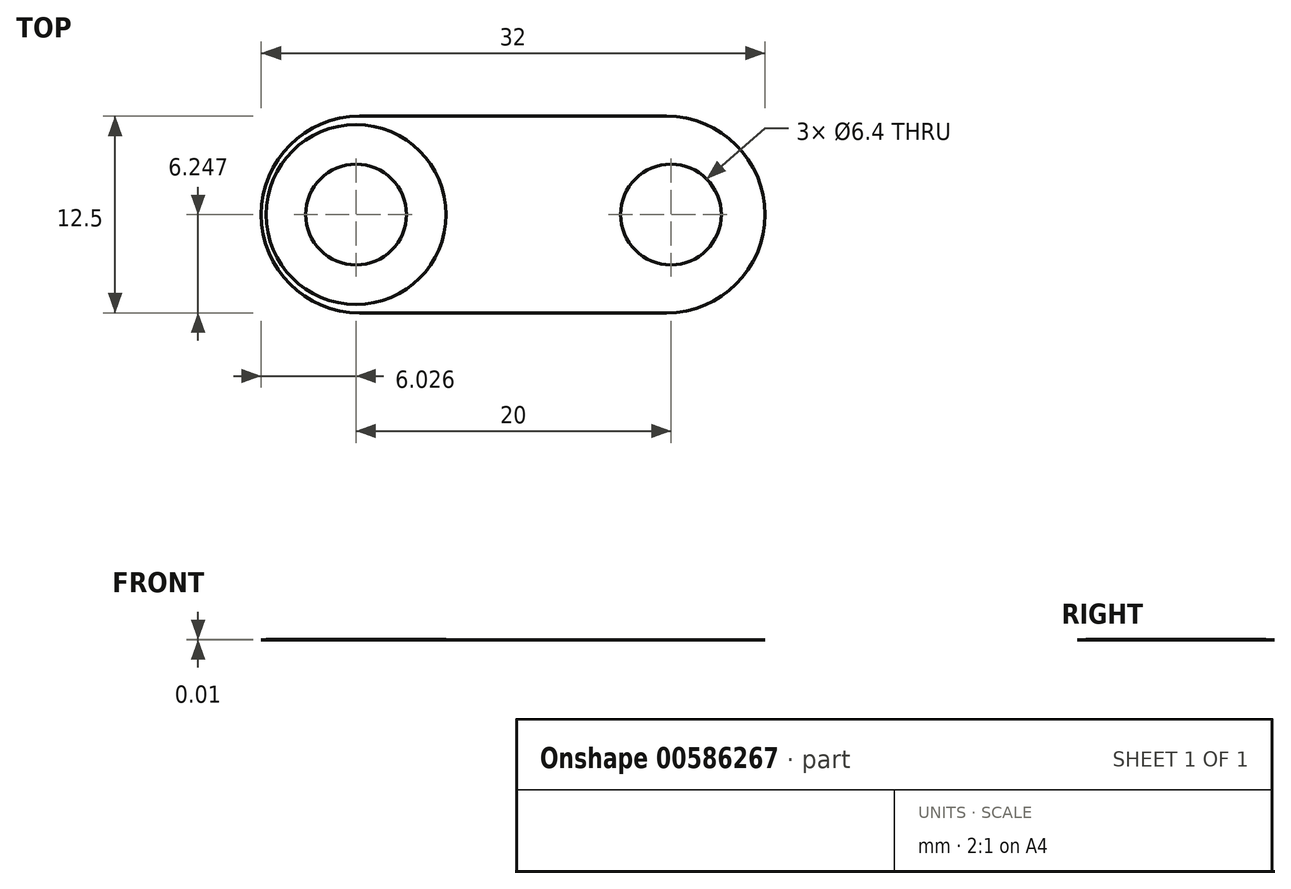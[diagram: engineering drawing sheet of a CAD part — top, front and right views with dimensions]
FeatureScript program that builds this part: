
annotation { "Feature Type Name" : "Feature", "Feature Type Description" : "" }
export const myFeature = defineFeature(function(context is Context, id is Id, definition is map)
    precondition{}
    {
        {
            var Q0;
            Q0=qCreatedBy(makeId("Top.planeOp"),FACE);
            var sketch = newSketch(context, id + "F0", { "sketchPlane" : qUnion([Q0])});
            skLineSegment(sketch, "E0", {"start": v(-5.4, 37.78) * mm, "end": v(14.1, 37.78) * mm});
            skLineSegment(sketch, "E1", {"start": v(-5.4, 50.28) * mm, "end": v(14.1, 50.28) * mm});
            skArc(sketch, "E2", {"start": v(-5.4, 50.28) * mm, "mid": v(-11.66, 44.03) * mm, "end": v(-5.4, 37.78) * mm});
            skArc(sketch, "E3", {"start": v(14.1, 37.78) * mm, "mid": v(20.34, 44.03) * mm, "end": v(14.1, 50.28) * mm});
            skCircle(sketch, "E4", {"center": v(-5.63, 44.03) * mm, "radius": 3.2 * mm});
            skCircle(sketch, "E5", {"center": v(14.37, 44.03) * mm, "radius": 3.2 * mm});
            skSolve(sketch);
        }
        {
            var Q0;
            Q0=makeQuery(id+"F0.imprint","IMPRINT",FACE,{"disambiguationData":[TD([[makeQuery(id+"F0.imprint","IMPRINT",EDGE,{"derivedFrom":sQuery(id+"F0.wireOp",EDGE,"E0")}),1.0]])]});
            extrude(context, id + "F1", {"entities" : qUnion([Q0]), "depth" : 1 / 203.2 * mm, "offsetDistance" : 25 * mm});
        }
        {
            var Q0;
            Q0=makeQuery(id+"F1.opExtrude","CAP_FACE",FACE,{"disambiguationData":[OSD([sQuery(id+"F0.wireOp",EDGE,"E0"),sQuery(id+"F0.wireOp",EDGE,"E1"),sQuery(id+"F0.wireOp",EDGE,"E2"),sQuery(id+"F0.wireOp",EDGE,"E3"),sQuery(id+"F0.wireOp",EDGE,"E4"),sQuery(id+"F0.wireOp",EDGE,"E5")])],"isStart":false});
            var sketch = newSketch(context, id + "F2", { "sketchPlane" : qUnion([Q0])});
            skCircle(sketch, "E6", {"center": v(-5.63, 44.03) * mm, "radius": 5.72 * mm});
            skCircle(sketch, "E7", {"center": v(-5.63, 44.03) * mm, "radius": 3.2 * mm});
            skSolve(sketch);
        }
        {
            var Q0;
            Q0 = qSketchRegion(id + "F2", true);
            extrude(context, id + "F3", {"entities" : qUnion([Q0]), "depth" : 1 / 101.6 * mm, "offsetDistance" : 25 * mm});
        }
    });
